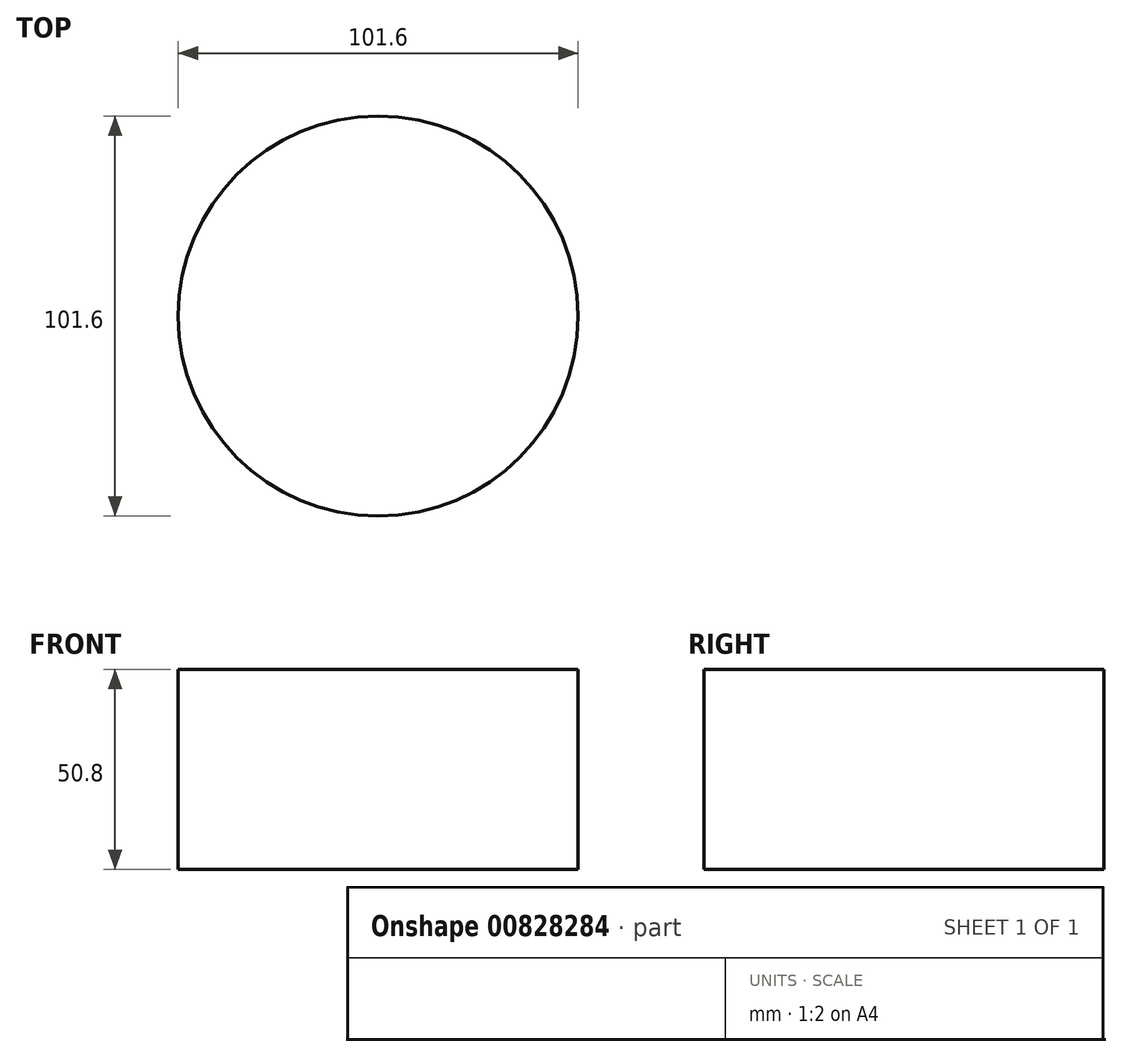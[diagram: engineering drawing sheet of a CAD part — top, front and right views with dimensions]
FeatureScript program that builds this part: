
annotation { "Feature Type Name" : "Feature", "Feature Type Description" : "" }
export const myFeature = defineFeature(function(context is Context, id is Id, definition is map)
    precondition{}
    {
        {
            var Q0;
            Q0=qCreatedBy(makeId("Top.planeOp"),FACE);
            var sketch = newSketch(context, id + "F0", { "sketchPlane" : qUnion([Q0])});
            skCircle(sketch, "E0", {"center": v(0, 0) * mm, "radius": 50.8 * mm});
            skSolve(sketch);
        }
        {
            var Q0;
            Q0 = qSketchRegion(id + "F0", true);
            extrude(context, id + "F1", {"entities" : qUnion([Q0]), "depth" : 50.8 * mm, "offsetDistance" : 25.4 * mm});
        }
    });
